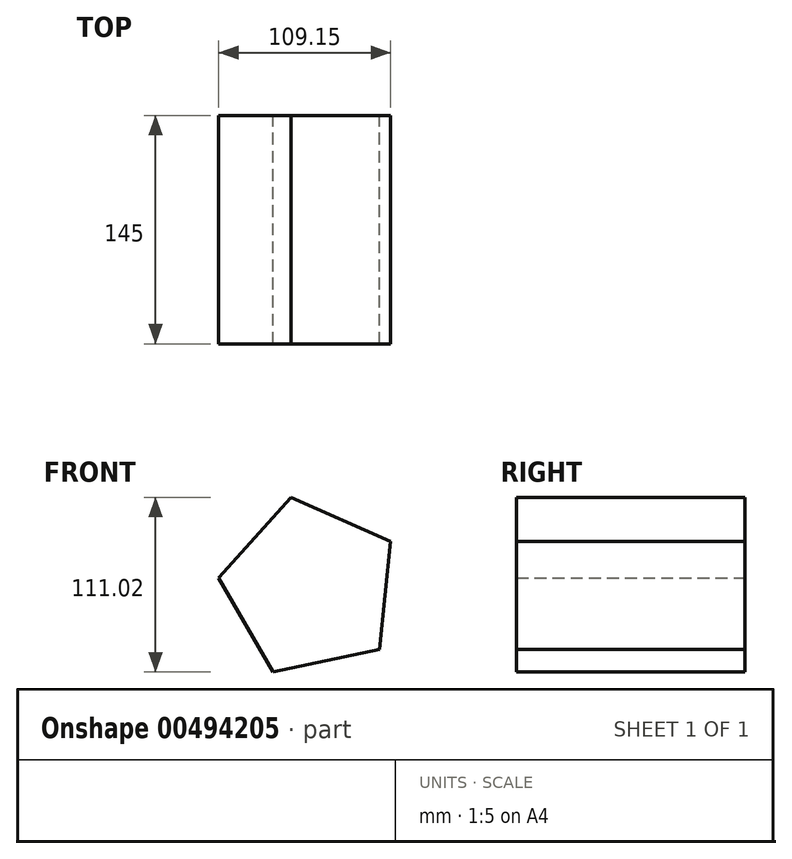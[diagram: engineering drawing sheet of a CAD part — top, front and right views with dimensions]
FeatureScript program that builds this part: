
annotation { "Feature Type Name" : "Feature", "Feature Type Description" : "" }
export const myFeature = defineFeature(function(context is Context, id is Id, definition is map)
    precondition{}
    {
        {
            var Q0;
            Q0=qCreatedBy(makeId("Front.planeOp"),FACE);
            var sketch = newSketch(context, id + "F0", { "sketchPlane" : qUnion([Q0])});
            skCircle(sketch, "E0.cCircle", {"center": v(0, 0) * mm, "radius": 58.68 * mm, "construction": true});
            skLineSegment(sketch, "E0.0", {"start": v(50.78, 29.4) * mm, "end": v(43.66, -39.2) * mm});
            skLineSegment(sketch, "E0.1", {"start": v(43.66, -39.2) * mm, "end": v(-23.8, -53.64) * mm});
            skLineSegment(sketch, "E0.2", {"start": v(-23.8, -53.64) * mm, "end": v(-58.37, 6.06) * mm});
            skLineSegment(sketch, "E0.3", {"start": v(-58.37, 6.06) * mm, "end": v(-12.28, 57.38) * mm});
            skLineSegment(sketch, "E0.4", {"start": v(-12.28, 57.38) * mm, "end": v(50.78, 29.4) * mm});
            skSolve(sketch);
        }
        {
            var Q0;
            Q0=makeQuery(id+"F0.imprint","IMPRINT",FACE,{"disambiguationData":[TD([[makeQuery(id+"F0.imprint","IMPRINT",EDGE,{"derivedFrom":sQuery(id+"F0.wireOp",EDGE,"E0.0")}),-1.0]])]});
            extrude(context, id + "F1", {"entities" : qUnion([Q0]), "depth" : 145 * mm});
        }
    });
